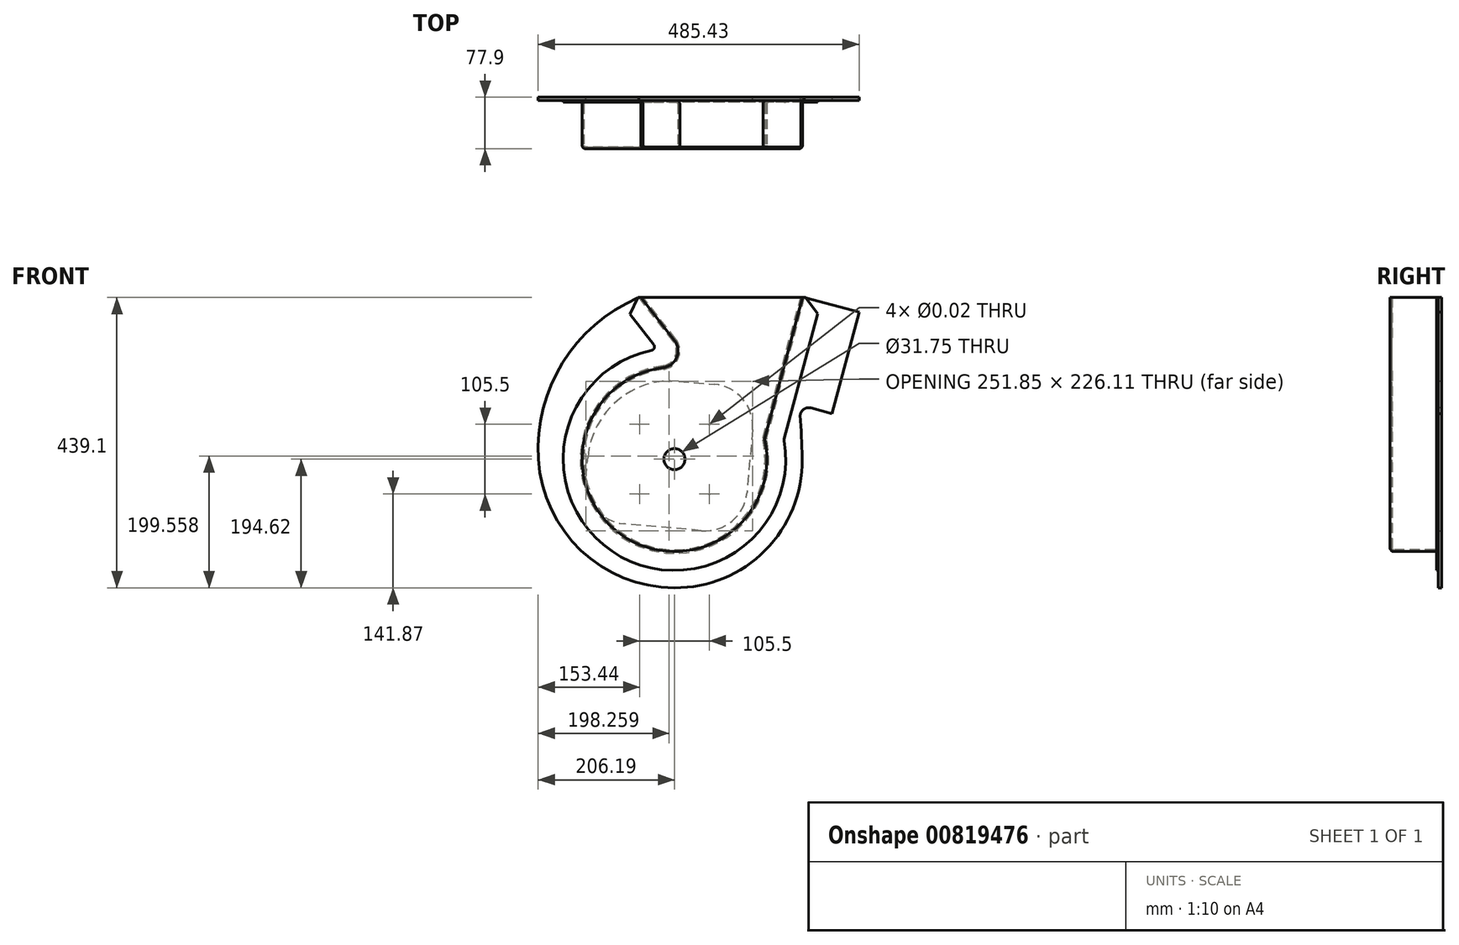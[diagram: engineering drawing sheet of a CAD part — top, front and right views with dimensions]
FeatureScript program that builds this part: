
annotation { "Feature Type Name" : "Feature", "Feature Type Description" : "" }
export const myFeature = defineFeature(function(context is Context, id is Id, definition is map)
    precondition{}
    {
        {
            var Q0;
            Q0=qCreatedBy(makeId("Front.planeOp"),FACE);
            var sketch = newSketch(context, id + "F0", { "sketchPlane" : qUnion([Q0])});
            skCircle(sketch, "E0", {"center": v(0, 0) * mm, "radius": 15.88 * mm, "construction": true});
            skLineSegment(sketch, "E1", {"start": v(0, 0) * mm, "end": v(0, 47.55) * mm, "construction": true});
            skLineSegment(sketch, "E2", {"start": v(0, 0) * mm, "end": v(-52.75, 52.75) * mm, "construction": true});
            skLineSegment(sketch, "E3", {"start": v(0, 0) * mm, "end": v(-43.33, 0) * mm, "construction": true});
            skPoint(sketch, "E4", {"position": v(-52.75, 52.75) * mm});
            skPoint(sketch, "E5.MirrorP", {"position": v(52.75, 52.75) * mm});
            skPoint(sketch, "E6.MirrorP", {"position": v(-52.75, -52.75) * mm});
            skPoint(sketch, "E7.MirrorP", {"position": v(52.75, -52.75) * mm});
            skArc(sketch, "E8", {"start": v(-16.93, 138.67) * mm, "mid": v(-80.57, -114.13) * mm, "end": v(136.33, 30.48) * mm});
            skLineSegment(sketch, "E9", {"start": v(-50.8, 244.48) * mm, "end": v(193.67, 244.48) * mm});
            skLineSegment(sketch, "E10", {"start": v(193.67, 244.48) * mm, "end": v(136.33, 30.48) * mm});
            skLineSegment(sketch, "E11", {"start": v(-50.8, 244.48) * mm, "end": v(0, 179.53) * mm});
            skArc(sketch, "E12", {"start": v(-16.93, 138.67) * mm, "mid": v(3.46, 154.16) * mm, "end": v(0, 179.53) * mm});
            skSolve(sketch);
        }
        {
            var Q0;
            Q0 = qSketchRegion(id + "F0", true);
            extrude(context, id + "F1", {"entities" : qUnion([Q0]), "oppositeDirection" : true, "depth" : 73.02 * mm, "offsetDistance" : 25.4 * mm});
        }
        {
            var Q0;
            Q0=makeQuery(id+"F1.opExtrude","CAP_FACE",FACE,{"disambiguationData":[OSD([sQuery(id+"F0.wireOp",EDGE,"E8"),sQuery(id+"F0.wireOp",EDGE,"E9"),sQuery(id+"F0.wireOp",EDGE,"E10"),sQuery(id+"F0.wireOp",EDGE,"E11"),sQuery(id+"F0.wireOp",EDGE,"E12")])],"isStart":false});
            var sketch = newSketch(context, id + "F2", { "sketchPlane" : qUnion([Q0])});
            skLineSegment(sketch, "E13.1", {"start": v(25.9, 166.27) * mm, "end": v(87.08, 244.47) * mm});
            skArc(sketch, "E13.2", {"start": v(-165.66, 29.53) * mm, "mid": v(97.76, -136.96) * mm, "end": v(25.9, 166.27) * mm});
            skLineSegment(sketch, "E13.3", {"start": v(-223.26, 244.48) * mm, "end": v(-165.66, 29.53) * mm});
            skLineSegment(sketch, "E14.0", {"start": v(87.08, 244.48) * mm, "end": v(-223.26, 244.48) * mm});
            skPoint(sketch, "E15.orphan", {"position": v(50.8, 244.48) * mm});
            skPoint(sketch, "E16.orphan", {"position": v(-193.67, 244.48) * mm});
            skSolve(sketch);
        }
        {
            var Q0;
            Q0 = qSketchRegion(id + "F2", true);
            extrude(context, id + "F3", {"entities" : qUnion([Q0]), "operationType" : NewBodyOperationType.ADD, "oppositeDirection" : true, "depth" : 2.67 * mm, "offsetDistance" : 25.4 * mm});
        }
        {
            var Q0;
            Q0=makeQuery(id+"F1.opExtrude","CAP_EDGE",EDGE,{"disambiguationData":[OSD([sQuery(id+"F0.wireOp",EDGE,"E10")])],"isStart":true});
            var Q1;
            Q1=makeQuery(id+"F1.opExtrude","CAP_EDGE",EDGE,{"disambiguationData":[OSD([sQuery(id+"F0.wireOp",EDGE,"E8")])],"isStart":true});
            var Q2;
            Q2=makeQuery(id+"F1.opExtrude","SWEPT_EDGE",EDGE,{"disambiguationData":[OSD([sQuery(id+"F0.wireOp",EDGE,"E8"),sQuery(id+"F0.wireOp",EDGE,"E10")])]});
            var Q3;
            Q3=makeQuery(id+"F3.opExtrude","SWEPT_EDGE",EDGE,{"disambiguationData":[OSD([sQuery(id+"F2.wireOp",EDGE,"E13.1"),sQuery(id+"F2.wireOp",EDGE,"E13.2")])]});
            var Q4;
            Q4=makeQuery(id+"F3.opExtrude","SWEPT_EDGE",EDGE,{"disambiguationData":[OSD([sQuery(id+"F2.wireOp",EDGE,"E13.2"),sQuery(id+"F2.wireOp",EDGE,"E13.3")])]});
            fillet(context, id + "F4", {"entities" : qUnion([Q0, Q1, Q2, Q3, Q4]), "radius" : 5.33 * mm, "tangentPropagation" : true, "allowEdgeOverflow" : false});
        }
        {
            var Q0;
            Q0=makeQuery(id+"F3.boolean.opBoolean","INTERSECT",EDGE,{"derivedFrom":[makeQuery(id+"F1.opExtrude","SWEPT_FACE",FACE,{"disambiguationData":[OSD([sQuery(id+"F0.wireOp",EDGE,"E11")])]}),makeQuery(id+"F3.opExtrude","CAP_FACE",FACE,{"disambiguationData":[OSD([sQuery(id+"F2.wireOp",EDGE,"E13.1"),sQuery(id+"F2.wireOp",EDGE,"E13.2"),sQuery(id+"F2.wireOp",EDGE,"E13.3"),sQuery(id+"F2.wireOp",EDGE,"E14.0")])],"isStart":false})]});
            fillet(context, id + "F5", {"entities" : qUnion([Q0]), "radius" : 2.67 * mm, "tangentPropagation" : true, "allowEdgeOverflow" : false});
        }
        {
            var Q0;
            Q0=makeQuery(id+"F1.opExtrude","SWEPT_FACE",FACE,{"disambiguationData":[OSD([sQuery(id+"F0.wireOp",EDGE,"E9")])]});
            var Q1;
            Q1=makeQuery(id+"F1.opExtrude","CAP_FACE",FACE,{"disambiguationData":[OSD([sQuery(id+"F0.wireOp",EDGE,"E0"),sQuery(id+"F0.wireOp",EDGE,"E8"),sQuery(id+"F0.wireOp",EDGE,"E9"),sQuery(id+"F0.wireOp",EDGE,"E10"),sQuery(id+"F0.wireOp",EDGE,"E11"),sQuery(id+"F0.wireOp",EDGE,"E12")])],"isStart":false});
            shell(context, id + "F6", {"entities" : qUnion([Q0, Q1]), "thickness" : 2.67 * mm});
        }
        {
            var Q0;
            Q0=sQuery(id+"F0.wireOp",VERTEX,"E4");
            var Q1;
            Q1=sQuery(id+"F0.wireOp",VERTEX,"E5.MirrorP");
            var Q2;
            Q2=sQuery(id+"F0.wireOp",VERTEX,"E7.MirrorP");
            var Q3;
            Q3=sQuery(id+"F0.wireOp",VERTEX,"E6.MirrorP");
            var Q4;
            Q4=makeQuery(id+"F1.opExtrude","SWEPT_BODY",BODY,{"disambiguationData":[OSD([sQuery(id+"F0.wireOp",EDGE,"E0"),sQuery(id+"F0.wireOp",EDGE,"E8"),sQuery(id+"F0.wireOp",EDGE,"E9"),sQuery(id+"F0.wireOp",EDGE,"E10"),sQuery(id+"F0.wireOp",EDGE,"E11"),sQuery(id+"F0.wireOp",EDGE,"E12")])]});
            hole(context, id + "F7", {"style" : HoleStyle.SIMPLE, "endStyle" : HoleEndStyle.THROUGH, "standardTappedOrClearance" : lookupTablePath({ "standard" : "ANSI", "size" : "25/64 (0.4)", "type" : "Drilled" }), "standardBlindInLast" : lookupTablePath({ "standard" : "ANSI", "size" : "25/64", "type" : "Drilled" }), "holeDiameter" : 25 / 1625.6 * mm, "majorDiameter" : 6.35 * mm, "tappedDepth" : 25.4 * mm, "tapClearance" : 3, "locations" : qUnion([Q0, Q1, Q2, Q3]), "scope" : qUnion([Q4]), "startStyle" : HoleStartStyle.SKETCH});
        }
        {
            var Q0;
            Q0=sQuery(id+"F0.wireOp",VERTEX,"E1.start");
            var Q1;
            Q1=makeQuery(id+"F1.opExtrude","SWEPT_BODY",BODY,{"disambiguationData":[OSD([sQuery(id+"F0.wireOp",EDGE,"E8"),sQuery(id+"F0.wireOp",EDGE,"E9"),sQuery(id+"F0.wireOp",EDGE,"E10"),sQuery(id+"F0.wireOp",EDGE,"E11"),sQuery(id+"F0.wireOp",EDGE,"E12")])]});
            hole(context, id + "F8", {"style" : HoleStyle.SIMPLE, "endStyle" : HoleEndStyle.THROUGH, "holeDiameter" : 31.75 * mm, "majorDiameter" : 6.35 * mm, "tappedDepth" : 25.4 * mm, "tapClearance" : 3, "locations" : qUnion([Q0]), "scope" : qUnion([Q1]), "startStyle" : HoleStartStyle.SKETCH});
        }
        {
            var Q0;
            Q0=makeQuery(id+"F3.boolean.opBoolean","MERGE",FACE,{"derivedFrom":[makeQuery(id+"F1.opExtrude","CAP_FACE",FACE,{"disambiguationData":[OSD([sQuery(id+"F0.wireOp",EDGE,"E8"),sQuery(id+"F0.wireOp",EDGE,"E9"),sQuery(id+"F0.wireOp",EDGE,"E10"),sQuery(id+"F0.wireOp",EDGE,"E11"),sQuery(id+"F0.wireOp",EDGE,"E12")])],"isStart":false}),makeQuery(id+"F3.opExtrude","CAP_FACE",FACE,{"disambiguationData":[OSD([sQuery(id+"F2.wireOp",EDGE,"E13.1"),sQuery(id+"F2.wireOp",EDGE,"E13.2"),sQuery(id+"F2.wireOp",EDGE,"E13.3"),sQuery(id+"F2.wireOp",EDGE,"E14.0")])],"isStart":true})]});
            var sketch = newSketch(context, id + "F9", { "sketchPlane" : qUnion([Q0])});
            skLineSegment(sketch, "E17", {"start": v(54.19, 244.48) * mm, "end": v(-196.44, 244.47) * mm});
            skLineSegment(sketch, "E18", {"start": v(-196.44, 244.47) * mm, "end": v(-279.24, 222.29) * mm});
            skLineSegment(sketch, "E19", {"start": v(-279.24, 222.29) * mm, "end": v(-238.15, 68.95) * mm});
            skLineSegment(sketch, "E20", {"start": v(-238.15, 68.95) * mm, "end": v(-206.08, 77.54) * mm});
            skLineSegment(sketch, "E21", {"start": v(0, 0) * mm, "end": v(0, -194.61) * mm, "construction": true});
            skLineSegment(sketch, "E22", {"start": v(0, 0) * mm, "end": v(205.74, 0) * mm, "construction": true});
            skLineSegment(sketch, "E23", {"start": v(0, 0) * mm, "end": v(-193.04, 0) * mm, "construction": true});
            skLineSegment(sketch, "E24", {"start": v(54.19, 244.48) * mm, "end": v(0, 0) * mm, "construction": true});
            skLineSegment(sketch, "E25", {"start": v(-196.44, 244.47) * mm, "end": v(0, 0) * mm, "construction": true});
            skLineSegment(sketch, "E26", {"start": v(0, 0) * mm, "end": v(0, 244.48) * mm, "construction": true});
            skArc(sketch, "E27", {"start": v(205.74, 0) * mm, "mid": v(168.79, 146.3) * mm, "end": v(54.19, 244.47) * mm});
            skArc(sketch, "E28", {"start": v(0, -194.61) * mm, "mid": v(141.34, -137.98) * mm, "end": v(205.74, 0) * mm});
            skArc(sketch, "E29", {"start": v(-193.04, 0) * mm, "mid": v(-137.32, -137.78) * mm, "end": v(0, -194.61) * mm});
            skArc(sketch, "E30", {"start": v(-206.08, 77.54) * mm, "mid": v(-194.68, 75.04) * mm, "end": v(-190.13, 64.29) * mm});
            skArc(sketch, "E31", {"start": v(-190.13, 64.29) * mm, "mid": v(-192.1, 32.17) * mm, "end": v(-193.04, 0) * mm});
            skSolve(sketch);
        }
        {
            var Q0;
            Q0 = qSketchRegion(id + "F9", true);
            extrude(context, id + "F10", {"entities" : qUnion([Q0]), "operationType" : NewBodyOperationType.ADD, "depth" : 4.88 * mm, "offsetDistance" : 25.4 * mm});
        }
        {
            var Q0;
            Q0=makeQuery(id+"F3.opExtrude","SWEPT_EDGE",EDGE,{"disambiguationData":[OSD([sQuery(id+"F2.wireOp",EDGE,"E13.3"),sQuery(id+"F2.wireOp",EDGE,"E14.0")])]});
            chamfer(context, id + "F11", {"entities" : qUnion([Q0]), "width" : 25.4 * mm});
        }
        {
            var Q0;
            Q0=makeQuery(id+"F3.opExtrude","SWEPT_EDGE",EDGE,{"disambiguationData":[OSD([sQuery(id+"F2.wireOp",EDGE,"E13.1"),sQuery(id+"F2.wireOp",EDGE,"E14.0")])]});
            chamfer(context, id + "F12", {"entities" : qUnion([Q0]), "width" : 31.75 * mm, "tangentPropagation" : true});
        }
        {
            var Q0;
            Q0=makeQuery(id+"F10.opExtrude","CAP_FACE",FACE,{"disambiguationData":[OSD([sQuery(id+"F9.wireOp",EDGE,"E17"),sQuery(id+"F9.wireOp",EDGE,"E18"),sQuery(id+"F9.wireOp",EDGE,"E19"),sQuery(id+"F9.wireOp",EDGE,"E20"),sQuery(id+"F9.wireOp",EDGE,"E27"),sQuery(id+"F9.wireOp",EDGE,"E28"),sQuery(id+"F9.wireOp",EDGE,"E29"),sQuery(id+"F9.wireOp",EDGE,"E30"),sQuery(id+"F9.wireOp",EDGE,"E31")])],"isStart":false});
            var sketch = newSketch(context, id + "F13", { "sketchPlane" : qUnion([Q0])});
            skLineSegment(sketch, "E32", {"start": v(-118, 44.5) * mm, "end": v(-109.7, -50.4) * mm});
            skLineSegment(sketch, "E33", {"start": v(-40.9, -108.12) * mm, "end": v(76.13, -97.88) * mm});
            skLineSegment(sketch, "E34", {"start": v(133.85, -29.08) * mm, "end": v(131.09, 2.54) * mm});
            skLineSegment(sketch, "E35", {"start": v(-6.5, 118) * mm, "end": v(-60.27, 113.29) * mm});
            skPoint(sketch, "E36.visualSharp", {"position": v(-104.16, -113.65) * mm});
            skArc(sketch, "E36.filletArc", {"start": v(-109.7, -50.4) * mm, "mid": v(-87.25, -93.5) * mm, "end": v(-40.9, -108.12) * mm});
            skPoint(sketch, "E37.visualSharp", {"position": v(-123.53, 107.75) * mm});
            skArc(sketch, "E37.filletArc", {"start": v(-60.27, 113.29) * mm, "mid": v(-103.38, 90.85) * mm, "end": v(-118, 44.5) * mm});
            skPoint(sketch, "E38.visualSharp", {"position": v(139.39, -92.34) * mm});
            skArc(sketch, "E38.filletArc", {"start": v(76.13, -97.88) * mm, "mid": v(119.24, -75.44) * mm, "end": v(133.85, -29.08) * mm});
            skPoint(sketch, "E39.visualSharp", {"position": v(120.02, 129.06) * mm});
            skArc(sketch, "E39.filletArc", {"start": v(131.09, 2.54) * mm, "mid": v(86.2, 88.76) * mm, "end": v(-6.5, 118) * mm});
            skLineSegment(sketch, "E40", {"start": v(0, 0) * mm, "end": v(0, 57.39) * mm, "construction": true});
            skSolve(sketch);
        }
        {
            var Q0;
            Q0 = qSketchRegion(id + "F13", true);
            var Q1;
            {var subQ0=sQuery(id+"F9.wireOp",EDGE,"E17");var subQ7=sQuery(id+"F0.wireOp",EDGE,"E9");var subQ10=sQuery(id+"F9.wireOp",EDGE,"E18");var subQ11=sQuery(id+"F9.wireOp",EDGE,"E27");Q1=makeQuery(id+"F10.boolean.opBoolean","SPLIT",FACE,{"disambiguationData":[TD([makeQuery(id+"F1.opExtrude","SWEPT_FACE",FACE,{"disambiguationData":[OSD([subQ7])]})])],"derivedFrom":makeQuery(id+"F10.opExtrude","CAP_FACE",FACE,{"disambiguationData":[OSD([subQ0,subQ10,sQuery(id+"F9.wireOp",EDGE,"E19"),sQuery(id+"F9.wireOp",EDGE,"E20"),subQ11,sQuery(id+"F9.wireOp",EDGE,"E28"),sQuery(id+"F9.wireOp",EDGE,"E29"),sQuery(id+"F9.wireOp",EDGE,"E30"),sQuery(id+"F9.wireOp",EDGE,"E31")])],"isStart":true})});}
            extrude(context, id + "F14", {"entities" : qUnion([Q0]), "operationType" : NewBodyOperationType.REMOVE, "endBound" : BoundingType.UP_TO_SURFACE, "oppositeDirection" : true, "depth" : 25.4 * mm, "endBoundEntityFace" : qUnion([Q1]), "offsetDistance" : 25.4 * mm});
        }
    });
